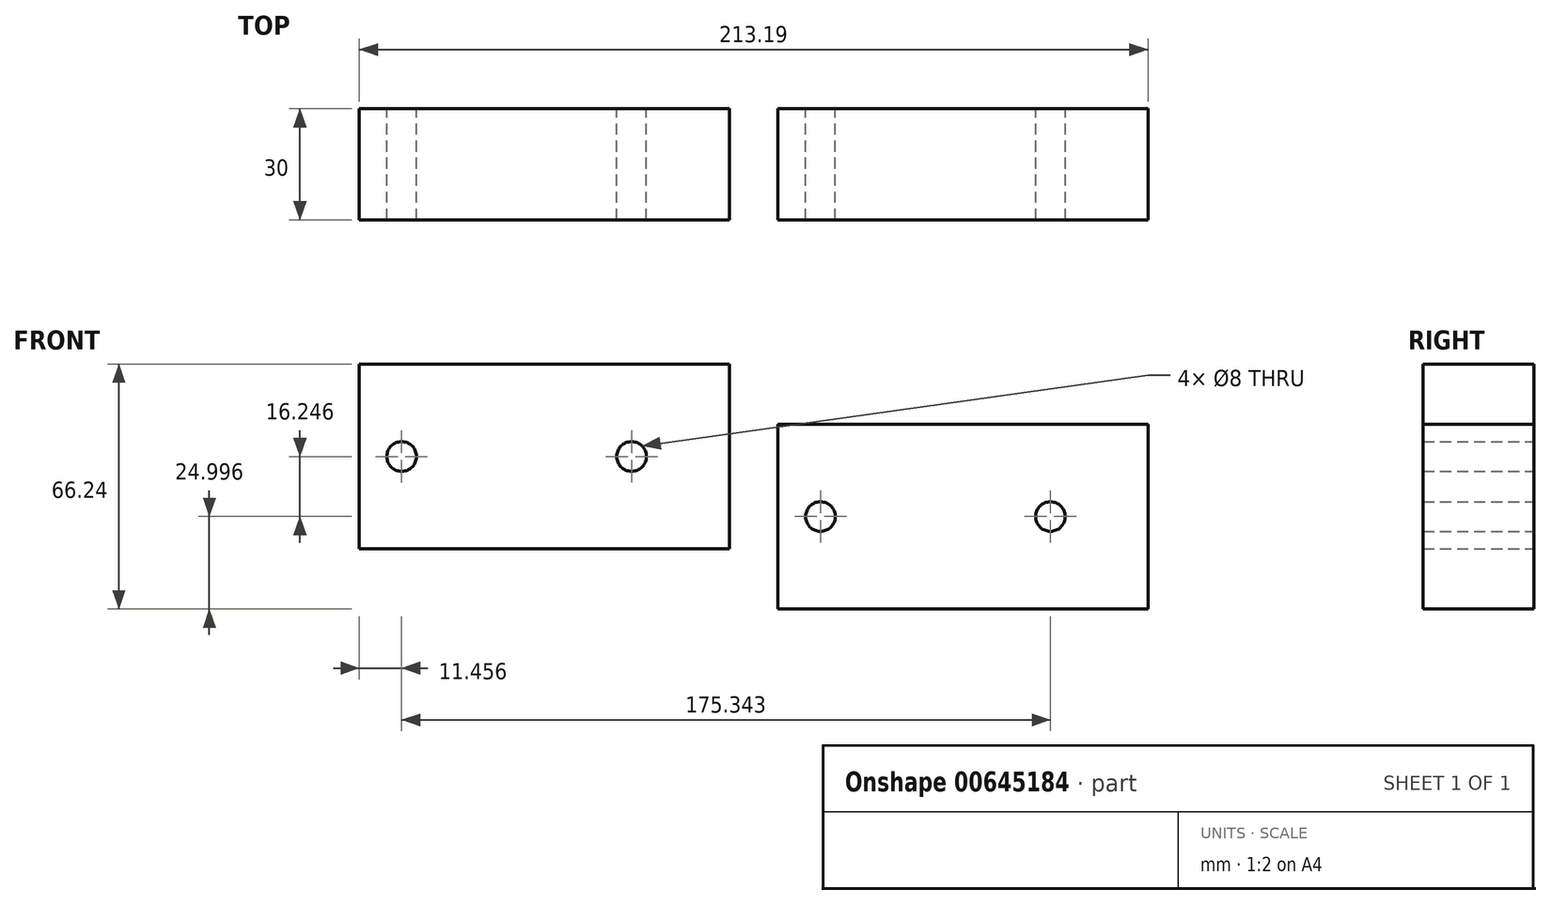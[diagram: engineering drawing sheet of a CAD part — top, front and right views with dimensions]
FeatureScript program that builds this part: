
annotation { "Feature Type Name" : "Feature", "Feature Type Description" : "" }
export const myFeature = defineFeature(function(context is Context, id is Id, definition is map)
    precondition{}
    {
        {
            var Q0;
            Q0=qCreatedBy(makeId("Front.planeOp"),FACE);
            var sketch = newSketch(context, id + "F0", { "sketchPlane" : qUnion([Q0])});
            skLineSegment(sketch, "E0.bottom", {"start": v(-128.78, 16.82) * mm, "end": v(-28.78, 16.82) * mm});
            skLineSegment(sketch, "E0.top", {"start": v(-128.78, -33.18) * mm, "end": v(-28.78, -33.18) * mm});
            skLineSegment(sketch, "E0.left", {"start": v(-128.78, 16.82) * mm, "end": v(-128.78, -33.18) * mm});
            skLineSegment(sketch, "E0.right", {"start": v(-28.78, 16.82) * mm, "end": v(-28.78, -33.18) * mm});
            skCircle(sketch, "E1", {"center": v(-117.32, -8.18) * mm, "radius": 4 * mm});
            skPoint(sketch, "E1.centerSnap0", {"position": v(-128.78, -8.18) * mm});
            skCircle(sketch, "E2", {"center": v(-55.18, -8.18) * mm, "radius": 4 * mm});
            skLineSegment(sketch, "E3.bottom", {"start": v(-15.59, 0.58) * mm, "end": v(84.41, 0.58) * mm});
            skLineSegment(sketch, "E3.top", {"start": v(-15.59, -49.42) * mm, "end": v(84.41, -49.42) * mm});
            skLineSegment(sketch, "E3.left", {"start": v(-15.59, 0.58) * mm, "end": v(-15.59, -49.42) * mm});
            skLineSegment(sketch, "E3.right", {"start": v(84.41, 0.58) * mm, "end": v(84.41, -49.42) * mm});
            skCircle(sketch, "E4", {"center": v(-4.13, -24.42) * mm, "radius": 4 * mm});
            skPoint(sketch, "E4.centerSnap0", {"position": v(-15.59, -24.42) * mm});
            skCircle(sketch, "E5", {"center": v(58.02, -24.42) * mm, "radius": 4 * mm});
            skSolve(sketch);
        }
        {
            var Q0;
            Q0 = qSketchRegion(id + "F0", true);
            extrude(context, id + "F1", {"entities" : qUnion([Q0]), "depth" : 30 * mm, "offsetDistance" : 25 * mm});
        }
    });
